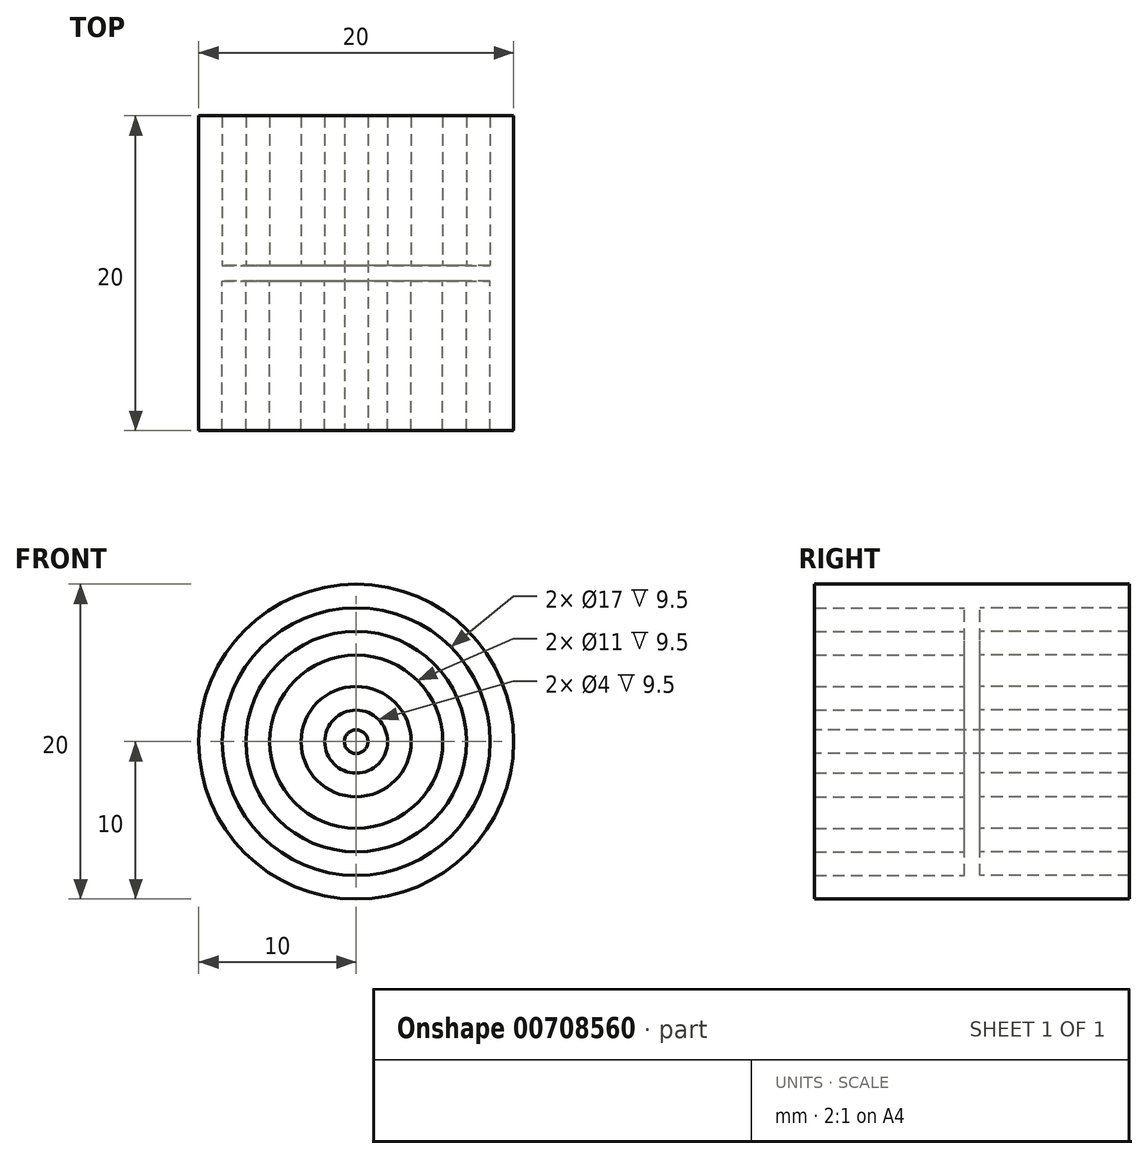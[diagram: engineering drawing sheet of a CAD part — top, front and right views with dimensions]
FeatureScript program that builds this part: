
annotation { "Feature Type Name" : "Feature", "Feature Type Description" : "" }
export const myFeature = defineFeature(function(context is Context, id is Id, definition is map)
    precondition{}
    {
        {
            var Q0;
            Q0=qCreatedBy(makeId("Front.planeOp"),FACE);
            var sketch = newSketch(context, id + "F0", { "sketchPlane" : qUnion([Q0])});
            skCircle(sketch, "E0", {"center": v(0, 0) * mm, "radius": 10 * mm});
            skCircle(sketch, "E1", {"center": v(0, 0) * mm, "radius": 8.5 * mm});
            skCircle(sketch, "E2", {"center": v(0, 0) * mm, "radius": 5.5 * mm});
            skCircle(sketch, "E3", {"center": v(0, 0) * mm, "radius": 2 * mm});
            skCircle(sketch, "E4", {"center": v(0, 0) * mm, "radius": 7 * mm});
            skCircle(sketch, "E5", {"center": v(0, 0) * mm, "radius": 3.5 * mm});
            skCircle(sketch, "E6", {"center": v(0, 0) * mm, "radius": 0.5 * mm});
            skSolve(sketch);
        }
        {
            var Q0;
            Q0=makeQuery(id+"F0.imprint","IMPRINT",FACE,{"disambiguationData":[TD([[makeQuery(id+"F0.imprint","IMPRINT",EDGE,{"derivedFrom":sQuery(id+"F0.wireOp",EDGE,"E6")}),1.0]])]});
            var sketch = newSketch(context, id + "F1", { "sketchPlane" : qUnion([Q0])});
            skCircle(sketch, "E7", {"center": v(0, 0) * mm, "radius": 10 * mm});
            skSolve(sketch);
        }
        {
            var Q0;
            Q0 = qSketchRegion(id + "F1", true);
            extrude(context, id + "F2", {"entities" : qUnion([Q0]), "depth" : 1 * mm, "offsetDistance" : 25 * mm});
        }
        {
            var Q0;
            Q0=makeQuery(id+"F0.imprint","IMPRINT",FACE,{"disambiguationData":[TD([[makeQuery(id+"F0.imprint","IMPRINT",EDGE,{"derivedFrom":sQuery(id+"F0.wireOp",EDGE,"E2")}),-1.0]])]});
            var Q1;
            Q1=makeQuery(id+"F0.imprint","IMPRINT",FACE,{"disambiguationData":[TD([[makeQuery(id+"F0.imprint","IMPRINT",EDGE,{"derivedFrom":sQuery(id+"F0.wireOp",EDGE,"E3")}),-1.0]])]});
            var Q2;
            Q2=makeQuery(id+"F0.imprint","IMPRINT",FACE,{"disambiguationData":[TD([[makeQuery(id+"F0.imprint","IMPRINT",EDGE,{"derivedFrom":sQuery(id+"F0.wireOp",EDGE,"E0")}),1.0]])]});
            extrude(context, id + "F3", {"entities" : qUnion([Q0, Q1, Q2]), "operationType" : NewBodyOperationType.ADD, "depth" : 10.5 * mm, "offsetDistance" : 25 * mm});
        }
        {
            var Q0;
            Q0 = qSketchRegion(id + "F0", true);
            extrude(context, id + "F4", {"entities" : qUnion([Q0]), "operationType" : NewBodyOperationType.ADD, "oppositeDirection" : true, "depth" : 9.5 * mm, "offsetDistance" : 25 * mm});
        }
        {
            var Q0;
            Q0=makeQuery(id+"F3.opExtrude","CAP_FACE",FACE,{"disambiguationData":[OSD([sQuery(id+"F0.wireOp",EDGE,"E3"),sQuery(id+"F0.wireOp",EDGE,"E5")])],"isStart":false});
            var Q1;
            Q1=makeQuery(id+"F3.opExtrude","CAP_FACE",FACE,{"disambiguationData":[OSD([sQuery(id+"F0.wireOp",EDGE,"E2"),sQuery(id+"F0.wireOp",EDGE,"E4")])],"isStart":false});
            var Q2;
            Q2=makeQuery(id+"F3.opExtrude","CAP_FACE",FACE,{"disambiguationData":[OSD([sQuery(id+"F0.wireOp",EDGE,"E0"),sQuery(id+"F0.wireOp",EDGE,"E1")])],"isStart":false});
            extrude(context, id + "F5", {"entities" : qUnion([Q0, Q1, Q2]), "operationType" : NewBodyOperationType.ADD, "oppositeDirection" : true, "depth" : 20 * mm, "offsetDistance" : 25 * mm});
        }
        {
            var Q0;
            Q0=makeQuery(id+"F3.opExtrude","CAP_FACE",FACE,{"disambiguationData":[OSD([sQuery(id+"F0.wireOp",EDGE,"E3"),sQuery(id+"F0.wireOp",EDGE,"E5")])],"isStart":false});
            var sketch = newSketch(context, id + "F6", { "sketchPlane" : qUnion([Q0])});
            skCircle(sketch, "E8", {"center": v(0, 0) * mm, "radius": 0.75 * mm});
            skSolve(sketch);
        }
        {
            var Q0;
            Q0=makeQuery(id+"F6.imprint","IMPRINT",FACE,{"disambiguationData":[TD([[makeQuery(id+"F6.imprint","IMPRINT",EDGE,{"derivedFrom":sQuery(id+"F6.wireOp",EDGE,"E8")}),1.0]])]});
            extrude(context, id + "F7", {"entities" : qUnion([Q0]), "oppositeDirection" : true, "depth" : 20 * mm, "offsetDistance" : 25 * mm});
        }
    });
